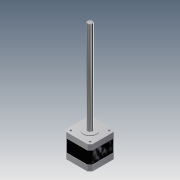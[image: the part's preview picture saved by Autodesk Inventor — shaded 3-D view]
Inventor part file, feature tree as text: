
AUTODESK INVENTOR PART (.ipt)
format: ipt  version: 2014 (Build 180170000, 170)  size: 166,912 bytes
history: native  units: mm
features: extrude x5, sketch x5, chamfer x1, projected_geometry x1
ambient origin geometry x8: Origin, YZ Plane, XZ Plane, XY Plane, X Axis, Y Axis, Z Axis, Center Point
bodies: Solid1 (feature_tree)
feature tree (12):
  extrude  "Extrusion1"  Depth=42.3mm
  chamfer  "Chamfer1"  Distance=9.0mm
  extrude  "Extrusion2"  Depth=0.5mm
  extrude  "Extrusion3"  Depth=0.5mm
  extrude  "Extrusion4"  Depth=20.0mm TaperAngle=0.0deg
  extrude  "Extrusion5"  Depth=9.0mm TaperAngle=0.0deg
  sketch  "Sketch1"  dims[d0=42.3mm d1=31.0mm]
  sketch  "Sketch3"  dims[d2=3.0mm d3=9.0mm d4=0.0mm]
  projected_geometry  "Projected Loop1"
  sketch  "Sketch4"  dims[d5=4.0mm d6=2.0mm d7=45.0deg d8=0.5mm]
  sketch  "Sketch5"  dims[d10=0.5mm d11=0.5mm]
  sketch  "Sketch6"  dims[d12=0.5mm d13=20.0mm d14=0.0mm d15=9.0mm d16=0.0mm d17=22.0mm d18=1.0mm d19=0.0mm d20=8.0mm d21=150.0mm d22=0.0mm]
